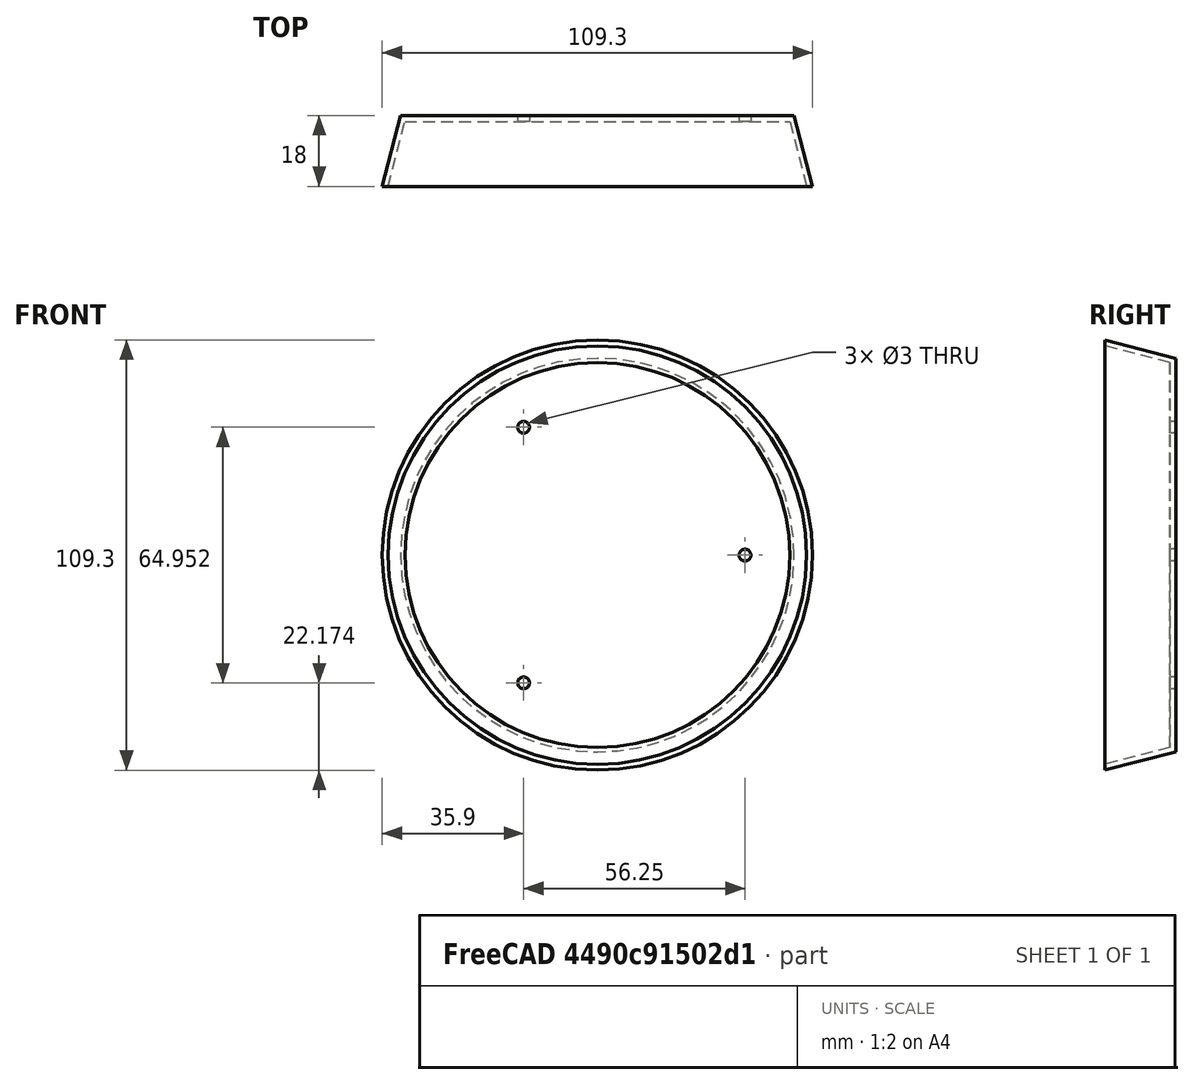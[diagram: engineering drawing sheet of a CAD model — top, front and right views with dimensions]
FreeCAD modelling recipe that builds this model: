
FCSTD DOCUMENT  (FreeCAD 0.18.4R)
Label: radiation_shield_dish_top
License: All rights reserved
LicenseURL: http://en.wikipedia.org/wiki/All_rights_reserved
objects: TechDraw::DrawViewDimension×3, Sketcher::SketchObject×2, PartDesign::Revolution×1, PartDesign::Hole×1, PartDesign::Body×1, App::Part×1, TechDraw::DrawSVGTemplate×1, TechDraw::DrawViewPart×1, TechDraw::DrawViewAnnotation×1, TechDraw::DrawPage×1
note: 7 computed .brp shape members not serialized (recipe doc carries the construction recipe); baked Part::Feature solids carry a one-line shape summary decoded from their .brp

FEATURE [Sketcher::SketchObject] Sketch
  sketch-geometry (6):
    g0: LineSegment StartX=-54.6463 StartY=0 StartZ=0 EndX=-53.1463 EndY=0 EndZ=0
    g1: LineSegment StartX=-53.1463 StartY=0 StartZ=0 EndX=-48.8872 EndY=16.5 EndZ=0
    g2: LineSegment StartX=-48.8872 StartY=16.5 StartZ=0 EndX=0 EndY=16.5 EndZ=0
    g3: LineSegment StartX=0 StartY=16.5 StartZ=0 EndX=0 EndY=18 EndZ=0
    g4: LineSegment StartX=0 StartY=18 StartZ=0 EndX=-50 EndY=18 EndZ=0
    g5: LineSegment StartX=-50 StartY=18 StartZ=0 EndX=-54.6463 EndY=0 EndZ=0
  constraints (18):
    c: Coincident(g0,g1)
    c: Coincident(g2,g3)
    c: Coincident(g3,g4)
    c: Coincident(g4,g5)
    c: PointOnObject(g2,g-2)
    c: PointOnObject(g3,g-2)
    c: PointOnObject(g0,g-1)
    c: Coincident(g5,g0)
    c: PointOnObject(g0,g-1)
    c: Equal(g0,g3)
    c: DistanceX(g0,g0) = 1.5
    c: Parallel(g4,g-1)
    c: Parallel(g2,g-1)
    c: Coincident(g1,g2)
    c: DistanceX(g4,g4) = 50
    c: Parallel(g5,g1)
    c: DistanceY(g-1,g4) = 18
    c: Distance(g0,g4) = 18.59
FEATURE [PartDesign::Revolution] Revolution
  Angle = 360
  Axis = (0,1,0)
  Base = (0,0,0)
  Profile = -> Sketch
  ReferenceAxis = -> Sketch [V_Axis]
FEATURE [Sketcher::SketchObject] Sketch001
  MapMode = 5
  Placement = pos=(0,18,0) rot=(0,0.707107,0.707107;3.14159rad)
  Support = -> [Revolution]
  sketch-geometry (7):
    g0: LineSegment [constr] StartX=18.75 StartY=32.476 StartZ=0 EndX=-37.5 EndY=0 EndZ=0
    g1: LineSegment [constr] StartX=-37.5 StartY=0 StartZ=0 EndX=18.75 EndY=-32.476 EndZ=0
    g2: LineSegment [constr] StartX=18.75 StartY=-32.476 StartZ=0 EndX=18.75 EndY=32.476 EndZ=0
    g3: Circle [constr] CenterX=0 CenterY=0 CenterZ=0 NormalX=0 NormalY=0 NormalZ=1 AngleXU=0 Radius=37.5
    g4: Circle CenterX=-37.5 CenterY=0 CenterZ=0 NormalX=0 NormalY=0 NormalZ=1 AngleXU=0 Radius=3
    g5: Circle CenterX=18.75 CenterY=32.476 CenterZ=0 NormalX=0 NormalY=0 NormalZ=1 AngleXU=0 Radius=3
    g6: Circle CenterX=18.75 CenterY=-32.476 CenterZ=0 NormalX=0 NormalY=0 NormalZ=1 AngleXU=0 Radius=3
  constraints (17):
    c: Coincident(g0,g1)
    c: Coincident(g1,g2)
    c: Coincident(g2,g0)
    c: Equal(g0,g1)
    c: Equal(g0,g2)
    c: PointOnObject(g0,g3)
    c: PointOnObject(g1,g3)
    c: PointOnObject(g2,g3)
    c: PointOnObject(g0,g-1)
    c: Coincident(g3,g-1)
    c: Radius(g3) = 37.5
    c: Radius(g5) = 3
    c: Coincident(g5,g0)
    c: Radius(g6) = 3
    c: Coincident(g6,g1)
    c: Radius(g4) = 3
    c: Coincident(g4,g0)
FEATURE [PartDesign::Hole] Hole
  BaseFeature = -> Revolution
  Depth = 25
  DepthType = 0
  Diameter = 3
  DrillPoint = 1
  DrillPointAngle = 118
  HoleCutCountersinkAngle = 90
  HoleCutDepth = 0
  HoleCutDiameter = 0
  HoleCutType = 0
  ModelActualThread = false
  Profile = -> Sketch001
  Tapered = false
  TaperedAngle = 90
  ThreadAngle = 0
  ThreadClass = 0
  ThreadCutOffInner = 0
  ThreadCutOffOuter = 0
  ThreadDirection = 0
  ThreadFit = 0
  ThreadPitch = 0
  ThreadSize = 0
  ThreadType = 0
  Threaded = false
FEATURE [PartDesign::Body] Body
  Group = -> [Sketch,Revolution,Sketch001,Hole]
  Origin = -> Origin001
  Tip = -> Hole
FEATURE [App::Part] Part
  Group = -> [Body]
  Origin = -> Origin
FEATURE [TechDraw::DrawSVGTemplate] Template
  EditableTexts = AUTHOR_NAME=Norman Rembarz; DN=DN; DRAWING_TITLE=RADIATION SHIELD - building instruction; FC-DATE=31/10/2020; FC-REV=REV A; FC-SC=1:1; FC-SH=1; FC-SI=A4; FreeCAD_DRAWING=top unit of radiation shield for weather sensor; PN=RS-TU-1; SI-5=REGREEN PROJECT of EU
  Height = 297
  Orientation = 0
  Width = 210
FEATURE [TechDraw::DrawViewPart] View  label="Draufsicht"
  CoarseView = false
  Direction = (0,1,0)
  Focus = 100
  HardHidden = false
  IsoCount = 0
  IsoHidden = false
  IsoVisible = false
  LockPosition = false
  Perspective = false
  Rotation = 0
  ScaleType = 0
  SeamHidden = false
  SeamVisible = false
  SmoothHidden = false
  SmoothVisible = false
  Source = -> [Body]
  X = 109.469
  Y = 189.406
FEATURE [TechDraw::DrawViewDimension] Dimension
  Arbitrary = false
  FormatSpec = ⌀%.2f
  LockPosition = false
  MeasureType = 1
  OverTolerance = 0
  References2D = -> [View]
  Rotation = 0
  ScaleType = 0
  Type = 5
  UnderTolerance = 0
  X = -56.375
  Y = 66
FEATURE [TechDraw::DrawViewDimension] Dimension001
  Arbitrary = false
  FormatSpec = ⌀%.2f
  LockPosition = false
  MeasureType = 1
  OverTolerance = 0
  References2D = -> [View]
  Rotation = 0
  ScaleType = 0
  Type = 5
  UnderTolerance = 0
  X = 68.5201
  Y = 62.1654
FEATURE [TechDraw::DrawViewDimension] Dimension002
  Arbitrary = false
  FormatSpec = %.2f
  LockPosition = false
  MeasureType = 1
  OverTolerance = 0
  References2D = -> [View]
  Rotation = 0
  ScaleType = 0
  Type = 0
  UnderTolerance = 0
  X = 7.30282
  Y = -20.3823
FEATURE [TechDraw::DrawViewAnnotation] Annotation
  Font = osifont
  LineSpace = 80
  LockPosition = false
  MaxWidth = -1
  Rotation = 0
  ScaleType = 0
  Text = part has same dimensions as Part No. RS-DU-1 only middle hole is not placed
  TextSize = 3
  TextStyle = 0
  X = 129.476
  Y = 88.2505
FEATURE [TechDraw::DrawPage] Page  label="Zeichnung"
  KeepUpdated = true
  ProjectionType = 0
  Template = -> Template
  Views = -> [View,Dimension,Dimension001,Dimension002,Annotation]
